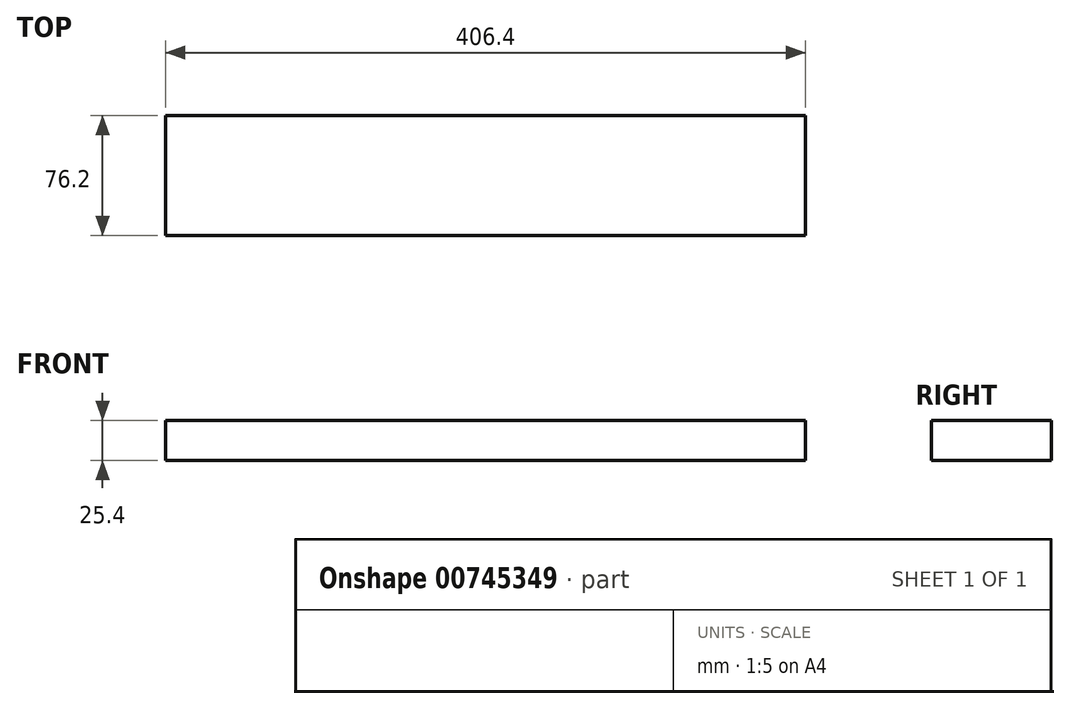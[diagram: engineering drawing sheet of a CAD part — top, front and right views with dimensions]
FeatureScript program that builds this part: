
annotation { "Feature Type Name" : "Feature", "Feature Type Description" : "" }
export const myFeature = defineFeature(function(context is Context, id is Id, definition is map)
    precondition{}
    {
        {
            var Q0;
            Q0=qCreatedBy(makeId("Top.planeOp"),FACE);
            var sketch = newSketch(context, id + "F0", { "sketchPlane" : qUnion([Q0])});
            skLineSegment(sketch, "E0.bottom", {"start": v(0, 0) * mm, "end": v(406.4, 0) * mm});
            skLineSegment(sketch, "E0.top", {"start": v(0, 76.2) * mm, "end": v(406.4, 76.2) * mm});
            skLineSegment(sketch, "E0.left", {"start": v(0, 0) * mm, "end": v(0, 76.2) * mm});
            skLineSegment(sketch, "E0.right", {"start": v(406.4, 0) * mm, "end": v(406.4, 76.2) * mm});
            skSolve(sketch);
        }
        {
            var Q0;
            Q0=makeQuery(id+"F0.imprint","IMPRINT",FACE,{"disambiguationData":[TD([[makeQuery(id+"F0.imprint","IMPRINT",EDGE,{"derivedFrom":sQuery(id+"F0.wireOp",EDGE,"E0.bottom")}),1.0]])]});
            extrude(context, id + "F1", {"entities" : qUnion([Q0]), "depth" : 25.4 * mm, "offsetDistance" : 25.4 * mm});
        }
    });
